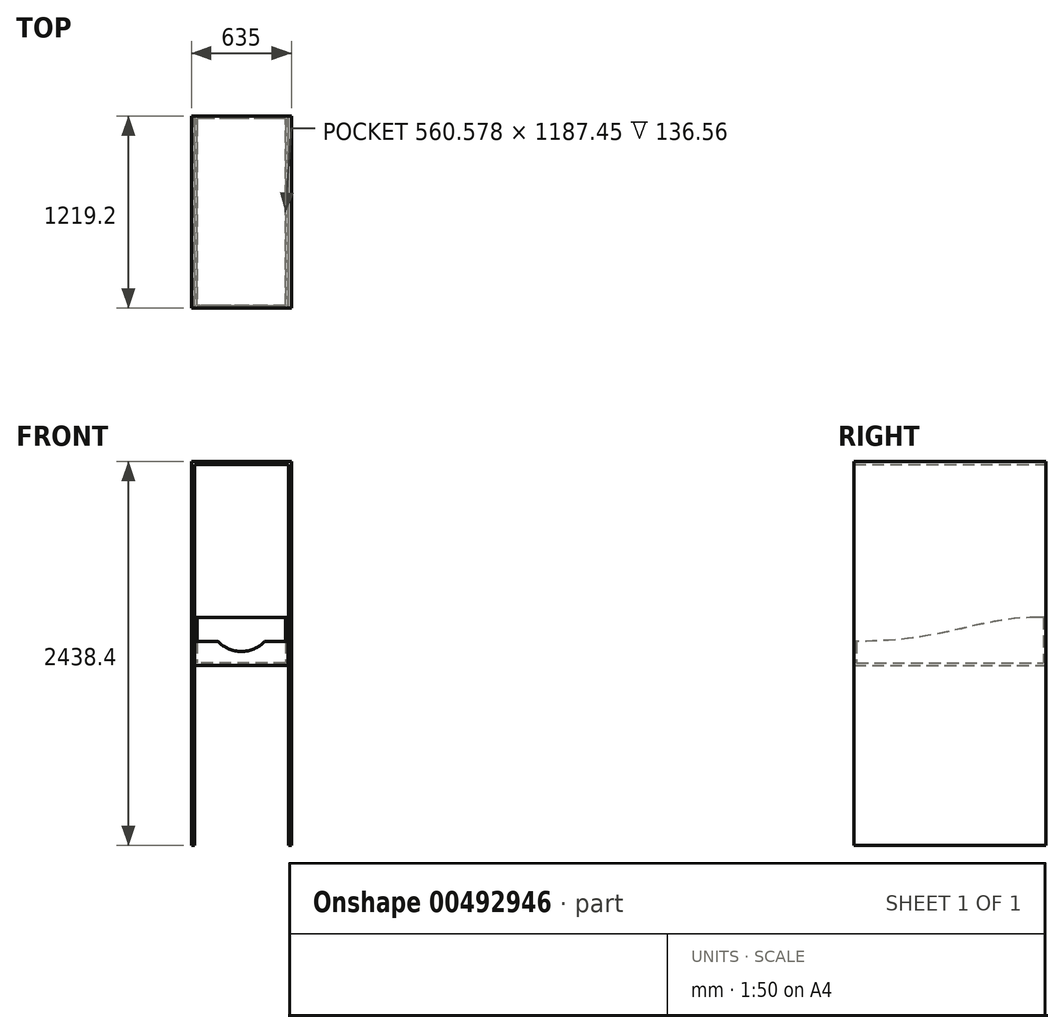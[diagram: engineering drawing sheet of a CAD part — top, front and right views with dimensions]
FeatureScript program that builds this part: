
annotation { "Feature Type Name" : "Feature", "Feature Type Description" : "" }
export const myFeature = defineFeature(function(context is Context, id is Id, definition is map)
    precondition{}
    {
        {
            var Q0;
            Q0=qCreatedBy(makeId("Front.planeOp"),FACE);
            var sketch = newSketch(context, id + "F0", { "sketchPlane" : qUnion([Q0])});
            skLineSegment(sketch, "E0.bottom", {"start": v(-317.5, 1219.2) * mm, "end": v(317.5, 1219.2) * mm});
            skLineSegment(sketch, "E0.top", {"start": v(-317.5, -1219.2) * mm, "end": v(317.5, -1219.2) * mm});
            skLineSegment(sketch, "E0.left", {"start": v(-317.5, 1219.2) * mm, "end": v(-317.5, -1219.2) * mm});
            skLineSegment(sketch, "E0.right", {"start": v(317.5, 1219.2) * mm, "end": v(317.5, -1219.2) * mm});
            skPoint(sketch, "E0.middle", {"position": v(0, 0) * mm});
            skLineSegment(sketch, "E1.bottom", {"start": v(-298.45, 1200.15) * mm, "end": v(298.45, 1200.15) * mm});
            skLineSegment(sketch, "E1.top", {"start": v(-298.45, -1219.2) * mm, "end": v(298.45, -1219.2) * mm});
            skLineSegment(sketch, "E1.left", {"start": v(-298.45, 1200.15) * mm, "end": v(-298.45, -1219.2) * mm});
            skLineSegment(sketch, "E1.right", {"start": v(298.45, 1200.15) * mm, "end": v(298.45, -1219.2) * mm});
            skPoint(sketch, "E1.middle", {"position": v(0, -9.52) * mm});
            skSolve(sketch);
        }
        {
            var Q0;
            Q0=makeQuery(id+"F0.imprint","IMPRINT",FACE,{"disambiguationData":[TD([[makeQuery(id+"F0.imprint","IMPRINT",EDGE,{"derivedFrom":sQuery(id+"F0.wireOp",EDGE,"E0.bottom")}),-1.0]])]});
            extrude(context, id + "F1", {"entities" : qUnion([Q0]), "depth" : 1219.2 * mm, "offsetDistance" : 25.4 * mm, "symmetric" : true});
        }
        {
            var Q0;
            Q0=qCreatedBy(makeId("Right.planeOp"),FACE);
            var sketch = newSketch(context, id + "F2", { "sketchPlane" : qUnion([Q0])});
            skLineSegment(sketch, "E2.bottom", {"start": v(-609.6, 76.2) * mm, "end": v(609.6, 76.2) * mm});
            skLineSegment(sketch, "E2.top", {"start": v(-609.6, -76.2) * mm, "end": v(609.6, -76.2) * mm});
            skLineSegment(sketch, "E2.left", {"start": v(-609.6, 76.2) * mm, "end": v(-609.6, -76.2) * mm});
            skLineSegment(sketch, "E2.right", {"start": v(609.6, 76.2) * mm, "end": v(609.6, -76.2) * mm});
            skPoint(sketch, "E2.middle", {"position": v(0, 0) * mm});
            skLineSegment(sketch, "E3", {"start": v(609.6, 76.2) * mm, "end": v(609.6, 228.6) * mm});
            skLineSegment(sketch, "E4", {"start": v(609.6, 228.6) * mm, "end": v(558.8, 228.6) * mm});
            skFitSpline(sketch, "E5", {"points": [v(558.8, 228.6) * mm, v(-609.6, 76.2) * mm], "startDerivative": vector(-1219.2, 0) * mm, "endDerivative": vector(-1828.8, 0) * mm});
            skSolve(sketch);
        }
        {
            var Q0;
            Q0 = qSketchRegion(id + "F2", true);
            extrude(context, id + "F3", {"entities" : qUnion([Q0]), "endBound" : BoundingType.UP_TO_NEXT, "depth" : 25.4 * mm, "hasOffset" : true, "offsetDistance" : 2.3 * mm, "hasSecondDirection" : true, "secondDirectionBound" : BoundingType.UP_TO_NEXT, "secondDirectionOppositeDirection" : true, "secondDirectionDepth" : 25.4 * mm, "hasSecondDirectionOffset" : true, "secondDirectionOffsetDistance" : 2.3 * mm});
        }
        {
            var Q0;
            Q0=makeQuery(id+"F3.opExtrude","SWEPT_FACE",FACE,{"disambiguationData":[OSD([sQuery(id+"F2.wireOp",EDGE,"E5")])]});
            var Q1;
            Q1=makeQuery(id+"F3.opExtrude","SWEPT_FACE",FACE,{"disambiguationData":[OSD([sQuery(id+"F2.wireOp",EDGE,"E4")])]});
            shell(context, id + "F4", {"entities" : qUnion([Q0, Q1]), "thickness" : 15.88 * mm});
        }
        {
            var Q0;
            Q0=makeQuery(id+"F3.opExtrude","SWEPT_FACE",FACE,{"disambiguationData":[OSD([sQuery(id+"F2.wireOp",EDGE,"E2.left")])]});
            var sketch = newSketch(context, id + "F5", { "sketchPlane" : qUnion([Q0])});
            skCircle(sketch, "E6", {"center": v(0, 215.9) * mm, "radius": 203.2 * mm});
            skSolve(sketch);
        }
        {
            var Q0;
            {var subQ0=sQuery(id+"F5.wireOp",EDGE,"E6");var subQ1=makeQuery(id+"F3.opExtrude","TWEAK_EDGE",EDGE,{"derivedFrom":[makeQuery(id+"F2.imprint","IMPRINT",EDGE,{"derivedFrom":sQuery(id+"F2.wireOp",EDGE,"E2.left")}),makeQuery(id+"F2.imprint","IMPRINT",EDGE,{"derivedFrom":sQuery(id+"F2.wireOp",EDGE,"E5")})]});var subQ2=makeQuery(id+"F5.imprint","INTERSECT",VERTEX,{"disambiguationData":[OD(0.0)],"derivedFrom":[subQ1,subQ0]});Q0=makeQuery(id+"F5.imprint","IMPRINT",FACE,{"disambiguationData":[TD([[makeQuery(id+"F5.imprint","IMPRINT",EDGE,{"disambiguationData":[TD([[subQ2,-1.0]])],"derivedFrom":subQ0}),1.0]])]});}
            var Q1;
            {var subQ0=sQuery(id+"F5.wireOp",EDGE,"E6");var subQ1=makeQuery(id+"F3.opExtrude","TWEAK_EDGE",EDGE,{"derivedFrom":[makeQuery(id+"F2.imprint","IMPRINT",EDGE,{"derivedFrom":sQuery(id+"F2.wireOp",EDGE,"E2.left")}),makeQuery(id+"F2.imprint","IMPRINT",EDGE,{"derivedFrom":sQuery(id+"F2.wireOp",EDGE,"E5")})]});var subQ2=makeQuery(id+"F5.imprint","INTERSECT",VERTEX,{"disambiguationData":[OD(0.0)],"derivedFrom":[subQ1,subQ0]});Q1=makeQuery(id+"F5.imprint","IMPRINT",FACE,{"disambiguationData":[TD([[makeQuery(id+"F5.imprint","IMPRINT",EDGE,{"disambiguationData":[TD([[subQ2,1.0]])],"derivedFrom":subQ0}),1.0]])]});}
            var Q2;
            Q2=makeQuery(id+"F4.opShell","OFFSET_FACE",FACE,{"disambiguationData":[OSD([sQuery(id+"F2.wireOp",EDGE,"E2.left")])]});
            extrude(context, id + "F6", {"entities" : qUnion([Q0, Q1]), "operationType" : NewBodyOperationType.REMOVE, "endBound" : BoundingType.UP_TO_SURFACE, "oppositeDirection" : true, "depth" : 25.4 * mm, "endBoundEntityFace" : qUnion([Q2]), "offsetDistance" : 25.4 * mm});
        }
    });
